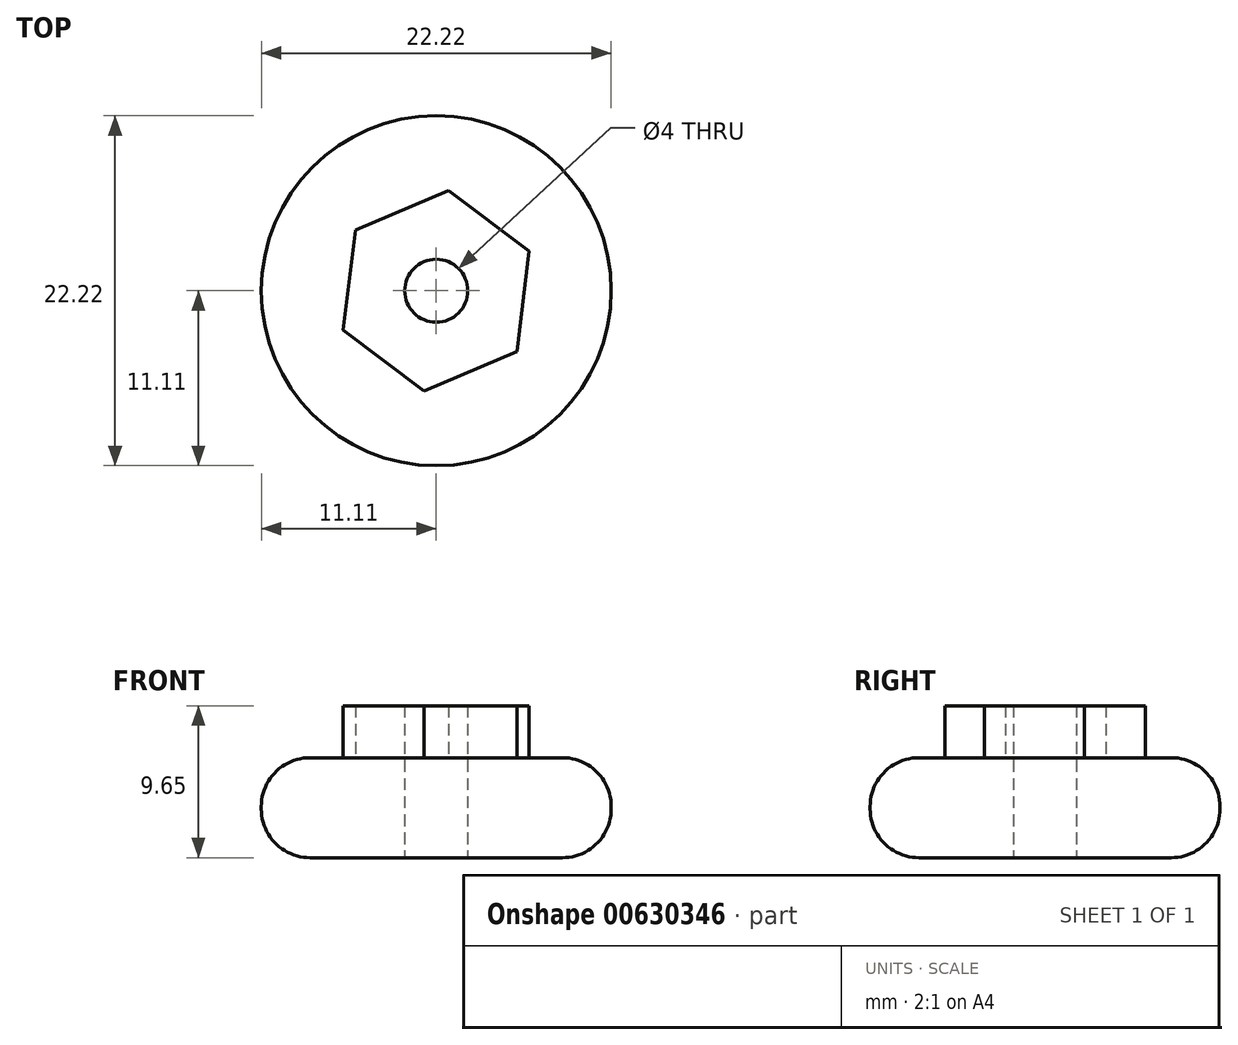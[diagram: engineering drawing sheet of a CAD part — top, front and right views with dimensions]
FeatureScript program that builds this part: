
annotation { "Feature Type Name" : "Feature", "Feature Type Description" : "" }
export const myFeature = defineFeature(function(context is Context, id is Id, definition is map)
    precondition{}
    {
        {
            var Q0;
            Q0=qCreatedBy(makeId("Top.planeOp"),FACE);
            var sketch = newSketch(context, id + "F0", { "sketchPlane" : qUnion([Q0])});
            skCircle(sketch, "E0", {"center": v(0, 0) * mm, "radius": 11.11 * mm});
            skCircle(sketch, "E1", {"center": v(0, 0) * mm, "radius": 2 * mm});
            skSolve(sketch);
        }
        {
            var Q0;
            Q0=makeQuery(id+"F0.imprint","IMPRINT",FACE,{"disambiguationData":[TD([[makeQuery(id+"F0.imprint","IMPRINT",EDGE,{"derivedFrom":sQuery(id+"F0.wireOp",EDGE,"E0")}),1.0]])]});
            extrude(context, id + "F1", {"entities" : qUnion([Q0]), "depth" : 6.35 * mm, "offsetDistance" : 25 * mm});
        }
        {
            var Q0;
            Q0=makeQuery(id+"F1.opExtrude","CAP_FACE",FACE,{"disambiguationData":[OSD([sQuery(id+"F0.wireOp",EDGE,"E0"),sQuery(id+"F0.wireOp",EDGE,"E1")])],"isStart":false});
            var sketch = newSketch(context, id + "F2", { "sketchPlane" : qUnion([Q0])});
            skCircle(sketch, "E2.cCircle", {"center": v(0, 0) * mm, "radius": 5.56 * mm, "construction": true});
            skLineSegment(sketch, "E2.0", {"start": v(-5.9, -2.5) * mm, "end": v(-5.12, 3.86) * mm});
            skLineSegment(sketch, "E2.1", {"start": v(-5.12, 3.86) * mm, "end": v(0.78, 6.37) * mm});
            skLineSegment(sketch, "E2.2", {"start": v(0.78, 6.37) * mm, "end": v(5.9, 2.5) * mm});
            skLineSegment(sketch, "E2.3", {"start": v(5.9, 2.5) * mm, "end": v(5.12, -3.86) * mm});
            skLineSegment(sketch, "E2.4", {"start": v(5.12, -3.86) * mm, "end": v(-0.78, -6.37) * mm});
            skLineSegment(sketch, "E2.5", {"start": v(-0.78, -6.37) * mm, "end": v(-5.9, -2.5) * mm});
            skPoint(sketch, "E2.0.midPoint", {"position": v(-5.51, 0.68) * mm});
            skSolve(sketch);
        }
        {
            var Q0;
            Q0=makeQuery(id+"F2.imprint","IMPRINT",FACE,{"disambiguationData":[TD([[makeQuery(id+"F2.imprint","IMPRINT",EDGE,{"derivedFrom":sQuery(id+"F2.wireOp",EDGE,"E2.0")}),-1.0]])]});
            extrude(context, id + "F3", {"entities" : qUnion([Q0]), "operationType" : NewBodyOperationType.ADD, "depth" : 3.3 * mm, "offsetDistance" : 25 * mm});
        }
        {
            var Q0;
            Q0=makeQuery(id+"F1.opExtrude","CAP_EDGE",EDGE,{"disambiguationData":[OSD([sQuery(id+"F0.wireOp",EDGE,"E0")])],"isStart":true});
            var Q1;
            Q1=makeQuery(id+"F1.opExtrude","CAP_EDGE",EDGE,{"disambiguationData":[OSD([sQuery(id+"F0.wireOp",EDGE,"E0")])],"isStart":false});
            fillet(context, id + "F4", {"entities" : qUnion([Q0, Q1]), "radius" : 3.1 * mm, "tangentPropagation" : true, "allowEdgeOverflow" : false});
        }
    });
